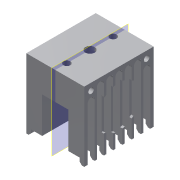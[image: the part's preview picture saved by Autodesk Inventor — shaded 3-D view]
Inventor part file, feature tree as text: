
AUTODESK INVENTOR PART (.ipt)
format: ipt  version: 2016 (Build 200138000, 138)  size: 499,712 bytes
history: native  units: mm
features: extrude x10, sketch x9, projected_geometry x7, thread x2, plane x2, mirror x2, reference x2, chamfer x1, fillet x1
ambient origin geometry x8: Origin, YZ Plane, XZ Plane, XY Plane, X Axis, Y Axis, Z Axis, Center Point
bodies: Solid1 (feature_tree)
feature tree (36):
  extrude  "Extrusion1"  Depth=7.0mm
  extrude  "Extrusion2"  Depth=30.0mm TaperAngle=0.0deg
  extrude  "Extrusion4"  Depth=1.5mm TaperAngle=0.0deg
  extrude  "Extrusion5"  Depth=3.0mm
  thread  "Thread1"  [1 undecoded]
  thread  "Thread2"  [1 undecoded]
  extrude  "Extrusion6"  Depth=3.0mm
  extrude  "Extrusion7"  Depth=3.0mm
  plane  "Work Plane1"
  extrude  "Extrusion9"  Depth=3.0mm
  mirror  "Mirror1"
  chamfer  "Chamfer1"  Distance=7.0mm
  extrude  "Extrusion11"  Depth=10.0mm TaperAngle=0.0deg
  extrude  "Extrusion12"  Depth=10.0mm TaperAngle=0.0deg
  mirror  "Mirror2"
  sketch  "Sketch13"  dims[d23=3.0mm d24=7.0mm d25=0.0mm d26=10.0mm d27=0.0mm d28=10.0mm d29=0.0mm d34=1.5mm d35=4.0mm d37=1.5mm d38=3.0mm d39=3.0mm d40=3.0mm d41=3.0mm d42=3.0mm d43=1.5mm d44=1.0mm d45=1.0mm d46=1.0mm d47=1.0mm d48=3.0mm d49=3.0mm d51=1.0mm d52=6.0mm d53=0.0mm d57=2.0mm d58=2.5mm d59=0.0mm d65=1.0mm d66=0.0mm d73=1.0mm d74=2.0mm d75=45.0deg d79=3.0mm d80=4.0mm d81=0.0mm d82=2.0mm d83=0.0mm d84=0.15mm d85=0.15mm d86=10.0mm d87=0.0mm d88=18.0mm d89=0.3mm]
  plane  "Work Plane2"
  extrude  "Extrusion13"  Depth=1.5mm
  fillet  "Fillet2"  Radius=4.0mm
  sketch  "Sketch1"  dims[d0=12.0mm d1=0.0mm d2=7.0mm]
  reference  "Reference1"
  sketch  "Sketch2"  dims[d3=7.0mm d4=30.0mm d5=0.0mm]
  sketch  "Sketch4"  dims[d9=4.1mm d10=1.5mm d11=0.0mm]
  sketch  "Sketch5"  dims[d12=3.0mm d13=2.4mm d14=3.0mm d15=2.4mm]
  sketch  "Sketch6"  dims[d16=3.0mm d17=3.0mm]
  sketch  "Sketch9"  dims[d18=3.0mm d19=3.0mm]
  sketch  "Sketch11"  dims[d20=3.0mm d21=3.0mm]
  projected_geometry  "Projected Loop1"
  projected_geometry  "Projected Loop2"
  projected_geometry  "Projected Loop3"
  sketch  "Sketch12"  dims[d22=3.0mm]
  projected_geometry  "Projected Loop4"
  projected_geometry  "Projected Loop5"
  projected_geometry  "Projected Loop6"
  projected_geometry  "Projected Loop7"
  reference  "Reference3"
note: 2 required parameter values undecoded (feature->parameter linkage not recoverable at this tier; creation-order binding heuristic only, values carry confidence <= 0.55)
